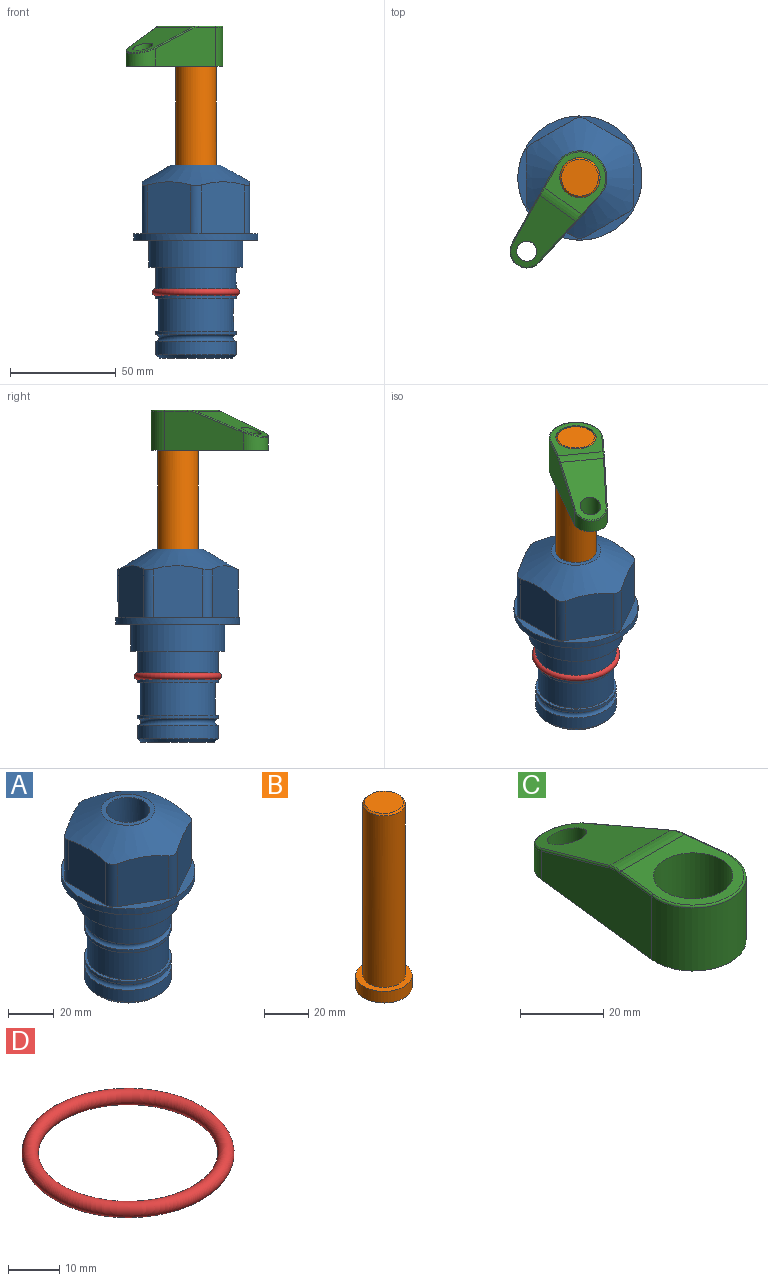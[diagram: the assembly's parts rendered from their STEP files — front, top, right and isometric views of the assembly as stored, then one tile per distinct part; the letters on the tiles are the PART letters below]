
ASSEMBLY  parts=4 mates=2
PART A: 36 faces, bbox 58.7x58.7x91.2 mm
  f0: cylinder r=17.78mm len=35.56mm, axis (0,0,1), area 1670.8mm2, adj f23,f24,f31
  f1: cylinder r=19.05mm len=38.1mm, axis (0,0,1), area 1191.9mm2, adj f26,f27,f30
  f2: plane 58.66x58.66mm, normal (0,0,-1), area 1150.6mm2, adj f3,f28
  f3: cylinder r=29.33mm len=58.66mm, axis (0,0,-1), area 585.1mm2, adj f2,f4
  f4: plane 58.66x58.66mm, normal (0,0,1), area 475.9mm2, adj f3,f5,f6,f7,f8,f9,f10,f11
  f5: plane 24.5x20.32mm, normal (-0.5,0.87,0), area 562.8mm2, adj f4,f15,f16,f17
  f6: plane 24.5x20.32mm, normal (0.5,0.87,0), area 562.8mm2, adj f4,f14,f15,f17
  f7: plane 24.5x23.48mm, normal (1,0,0), area 562.8mm2, adj f4,f13,f14,f17
  f8: plane 24.5x20.32mm, normal (0.5,-0.87,0), area 562.8mm2, adj f4,f12,f13,f17
  f9: plane 24.5x20.32mm, normal (-0.5,-0.87,0), area 562.8mm2, adj f4,f11,f12,f17
  f10: plane 24.5x23.48mm, normal (-1,0,0), area 562.8mm2, adj f4,f11,f16,f17
  f11: cylinder r=5.08mm len=23.01mm, axis (0,0,-1), area 121.2mm2, adj f4,f9,f10,f17
  f12: cylinder r=5.08mm len=23.01mm, axis (0,0,-1), area 121.2mm2, adj f4,f8,f9,f17
  f13: cylinder r=5.08mm len=23.01mm, axis (0,0,-1), area 121.2mm2, adj f4,f7,f8,f17
  f14: cylinder r=5.08mm len=23.01mm, axis (0,0,-1), area 121.2mm2, adj f4,f6,f7,f17
  f15: cylinder r=5.08mm len=23.01mm, axis (0,0,-1), area 121.2mm2, adj f4,f5,f6,f17
  f16: cylinder r=5.08mm len=23.01mm, axis (0,0,-1), area 121.2mm2, adj f4,f5,f10,f17
  f17: cone r=11.73mm half-angle=60deg, axis (0,0,-1), area 2071.8mm2, adj f5,f6,f7,f8,f9,f10,f11,f12
  f18: plane 23.46x23.46mm, normal (0,0,1), area 147.4mm2, adj f17,f35
  f19: plane 34.93x34.93mm, normal (0,0,-1), area 958mm2, adj f29
  f20: cylinder r=19.05mm len=38.1mm, axis (0,0,1), area 760.1mm2, adj f21,f29
  f21: torus R=19.05mm, axis (0,0,1), area 565.3mm2, adj f20,f22
  f22: cylinder r=19.05mm len=38.1mm, axis (0,0,1), area 190mm2, adj f21,f23
  f23: plane 38.1x38.1mm, normal (0,0,1), area 146.9mm2, adj f0,f22
  f24: plane 38.1x38.1mm, normal (0,0,-1), area 146.9mm2, adj f0,f25
  f25: cylinder r=19.05mm len=38.1mm, axis (0,0,1), area 190mm2, adj f24,f26
  f26: torus R=19.05mm, axis (0,0,1), area 565.3mm2, adj f1,f25
  f27: plane 44.45x44.45mm, normal (0,0,-1), area 411.7mm2, adj f1,f28
  f28: cylinder r=22.23mm len=44.45mm, axis (0,0,1), area 1773.5mm2, adj f2,f27
  f29: cone r=19.05mm half-angle=45deg, axis (0,0,1), area 257.5mm2, adj f19,f20
  f30: cylinder r=3.17mm len=6.75mm, axis (-1,0,0), area 128mm2, adj f1,f33
  f31: cylinder r=3.17mm len=6.35mm, axis (-1,0,0), area 102.5mm2, adj f0,f33
  f32: plane 25.4x25.4mm, normal (0,0,1), area 506.7mm2, adj f33
  f33: cylinder r=12.7mm len=66.42mm, axis (0,0,-1), area 5236.2mm2, adj f30,f31,f32,f34
  f34: cone r=9.53mm half-angle=30deg, axis (0,0,-1), area 443.4mm2, adj f33,f35
  f35: cylinder r=9.53mm len=19.05mm, axis (0,0,-1), area 849mm2, adj f18,f34
PART B: 6 faces, bbox 25.4x25.4x101.6 mm
  f0: plane 17.46x17.46mm, normal (0,0,1), area 239.5mm2, adj f5
  f1: plane 25.4x25.4mm, normal (0,0,-1), area 506.7mm2, adj f2
  f2: cylinder r=12.7mm len=25.4mm, axis (0,0,1), area 506.7mm2, adj f1,f3
  f3: plane 25.4x25.4mm, normal (0,0,1), area 221.7mm2, adj f2,f4
  f4: cylinder r=9.53mm len=94.46mm, axis (0,0,1), area 5653mm2, adj f3,f5
  f5: cone r=8.73mm half-angle=45deg, axis (0,0,-1), area 64.4mm2, adj f0,f4
PART C: 44 faces, bbox 27.5x64.5x19.1 mm
  f0: plane 2.3x0.95mm, normal (0,0,-1), area 1mm2, adj f25,f30,f34
  f1: plane 63.5x25.4mm, normal (0,0,-1), area 561.7mm2, adj f2,f3,f4,f5,f6,f7,f19,f20
  f2: cylinder r=12.7mm len=25.4mm, axis (0,0,-1), area 792.2mm2, adj f1,f3,f5,f13
  f3: plane 42.33x18.54mm, normal (0.99,0.11,0), area 647mm2, adj f1,f2,f4,f11,f12,f14
  f4: cylinder r=7.94mm len=15.78mm, axis (0,0,-1), area 158.6mm2, adj f1,f3,f5,f16
  f5: plane 42.33x18.54mm, normal (-0.99,0.11,0), area 647mm2, adj f1,f2,f4,f15,f17,f18
  f6: cylinder r=9.53mm len=19.05mm, axis (0,0,-1), area 1140.1mm2, adj f1,f8
  f7: cylinder r=4.76mm len=10.98mm, axis (0,0,-1), area 276.1mm2, adj f1,f9
  f8: plane 25.83x24.38mm, normal (0,0,1), area 262.2mm2, adj f6,f10,f11,f13,f15
  f9: plane 32.49x20.55mm, normal (0,0.34,0.94), area 489.9mm2, adj f7,f10,f14,f16,f18
  f10: cylinder r=12.7mm len=21.49mm, axis (-1,0,0), area 93.2mm2, adj f8,f9,f12,f17
  f11: cylinder r=0.51mm len=12.34mm, axis (0.11,-0.99,0), area 9.9mm2, adj f3,f8,f12,f13
  f12: bspline ~7.62x1.64mm, area 3.5mm2, adj f3,f10,f11,f14
  f13: torus R=12.19mm, axis (0,0,1), area 33.6mm2, adj f2,f8,f11,f15
  f14: cylinder r=0.51mm len=26.01mm, axis (0.1,-0.93,0.34), area 21.6mm2, adj f3,f9,f12,f16
  f15: cylinder r=0.51mm len=12.34mm, axis (0.11,0.99,0), area 9.9mm2, adj f5,f8,f13,f17
  f16: bspline ~15.78x7.05mm, area 15.7mm2, adj f4,f9,f14,f18
  f17: bspline ~7.62x1.64mm, area 3.5mm2, adj f5,f10,f15,f18
  f18: cylinder r=0.51mm len=26.01mm, axis (0.1,0.93,-0.34), area 21.6mm2, adj f5,f9,f16,f17
  f19: plane 21.6x14.29mm, normal (-0.99,-0.11,0), area 242.6mm2, adj f1,f26,f28,f34,f36,f38
  f20: plane 21.6x14.29mm, normal (0.99,-0.11,0), area 242.6mm2, adj f1,f27,f29,f37,f39,f41
  f21: cylinder r=12.7mm len=14.29mm, axis (0,0,-1), area 173.2mm2, adj f1,f26,f27,f30,f31,f33
  f22: cylinder r=7.94mm len=7.63mm, axis (0,0,-1), area 53.8mm2, adj f1,f28,f29,f42
  f23: plane 2.3x0.95mm, normal (0,0,-1), area 1mm2, adj f25,f33,f37
  f24: plane 17.94x12.32mm, normal (0,-0.34,-0.94), area 191.2mm2, adj f25,f38,f41,f42
  f25: cylinder r=9.53mm len=12.93mm, axis (-1,0,0), area 37.5mm2, adj f0,f23,f24,f31,f36,f39
  f26: cylinder r=1.59mm len=14.29mm, axis (0,0,-1), area 49mm2, adj f1,f19,f21,f32
  f27: cylinder r=1.59mm len=14.29mm, axis (0,0,-1), area 49mm2, adj f1,f20,f21,f35
  f28: cylinder r=1.59mm len=7.28mm, axis (0,0,-1), area 22.1mm2, adj f1,f19,f22,f40
  f29: cylinder r=1.59mm len=7.28mm, axis (0,0,-1), area 22.1mm2, adj f1,f20,f22,f43
  f30: torus R=14.29mm, axis (0,0,1), area 5.8mm2, adj f0,f21,f31,f32
  f31: bspline ~11.06x2.73mm, area 20.8mm2, adj f21,f25,f30,f33
  f32: sphere r=1.59mm, area 5.4mm2, adj f26,f30,f34
  f33: torus R=14.29mm, axis (0,0,1), area 5.8mm2, adj f21,f23,f31,f35
  f34: cylinder r=1.59mm len=1.68mm, axis (-0.11,0.99,0), area 2.4mm2, adj f0,f19,f32,f36
  f35: sphere r=1.59mm, area 5.4mm2, adj f27,f33,f37
  f36: bspline ~5.82x2.33mm, area 7.7mm2, adj f19,f25,f34,f38
  f37: cylinder r=1.59mm len=1.68mm, axis (0.11,0.99,0), area 2.4mm2, adj f20,f23,f35,f39
  f38: cylinder r=1.59mm len=18.33mm, axis (0.1,-0.93,0.34), area 46.7mm2, adj f19,f24,f36,f40
  f39: bspline ~5.82x2.33mm, area 7.7mm2, adj f20,f25,f37,f41
  f40: sphere r=1.59mm, area 3.6mm2, adj f28,f38,f42
  f41: cylinder r=1.59mm len=18.33mm, axis (0.1,0.93,-0.34), area 46.7mm2, adj f20,f24,f39,f43
  f42: bspline ~8.31x1.84mm, area 15.3mm2, adj f22,f24,f40,f43
  f43: sphere r=1.59mm, area 3.6mm2, adj f29,f41,f42
PART D: 1 faces, bbox 44.7x44.7x3.2 mm
  f0: torus R=19.05mm, axis (0,0,1), area 1193.9mm2
PLACE A at identity fixed
PLACE B rot(axis=(0,0,-1),125.9deg) t=(0,0,27.62)mm
PLACE C rot(axis=(0,0,1),144.1deg) t=(0,0,82.23)mm
PLACE D at identity
MATE cylindrical A.f0 <-> B.f2  axis (0,0,-1) through (0,0,25.78)mm
MATE fastened C.f2 <-> B.f2  axis (0,0,1) through (0,0,101.28)mm
